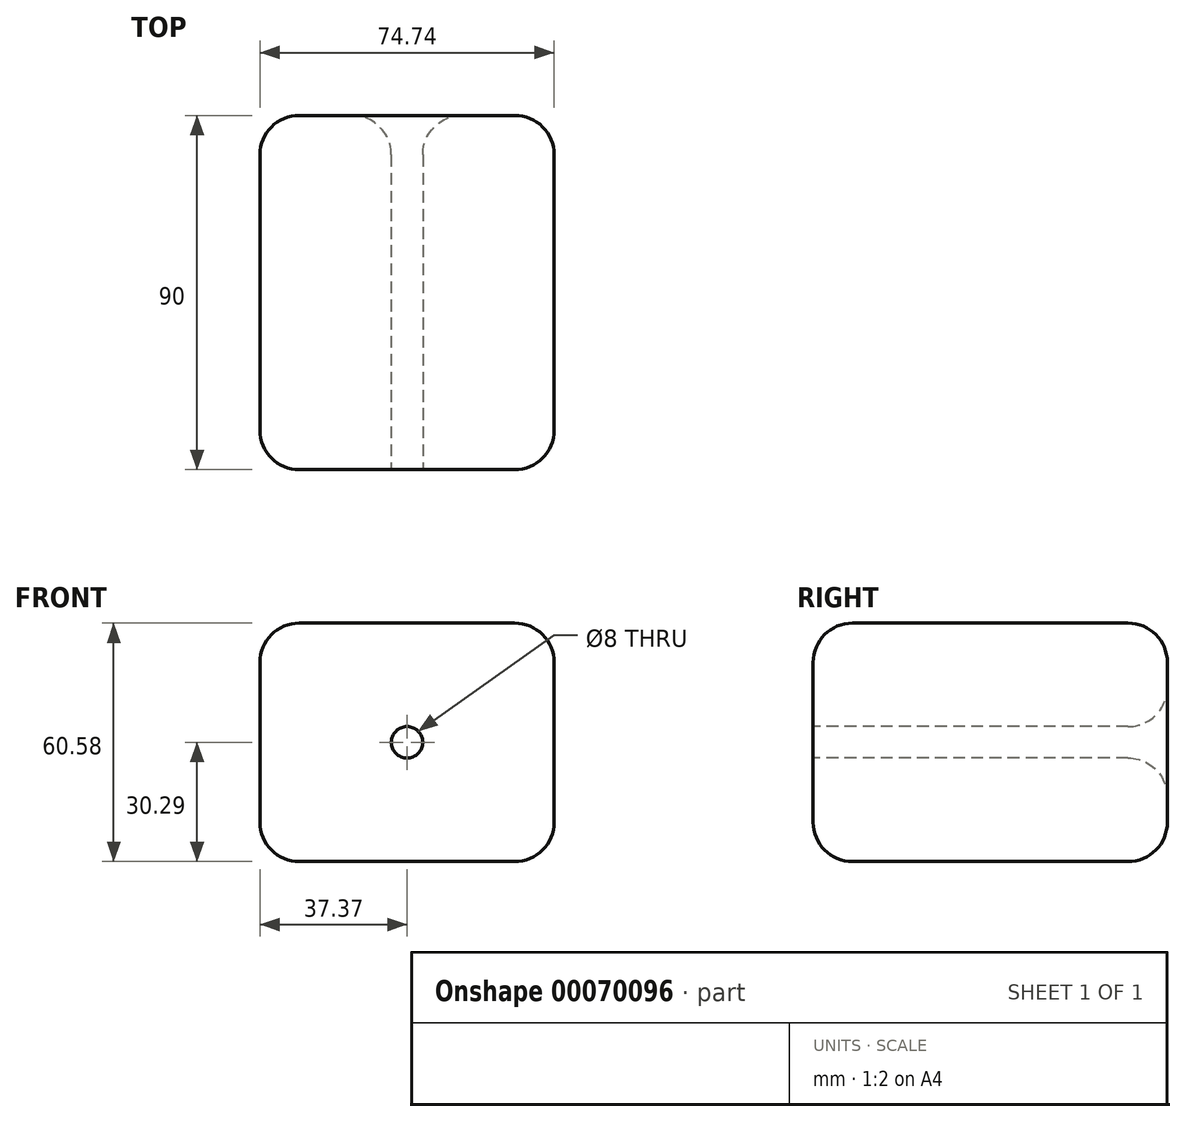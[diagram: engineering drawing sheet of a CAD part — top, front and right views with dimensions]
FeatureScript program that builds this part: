
annotation { "Feature Type Name" : "Feature", "Feature Type Description" : "" }
export const myFeature = defineFeature(function(context is Context, id is Id, definition is map)
    precondition{}
    {
        {
            var Q0;
            Q0=qCreatedBy(makeId("Front.planeOp"),FACE);
            var sketch = newSketch(context, id + "F0", { "sketchPlane" : qUnion([Q0])});
            skLineSegment(sketch, "E0.rect.bottom", {"start": v(-37.37, 30.29) * mm, "end": v(37.37, 30.29) * mm});
            skLineSegment(sketch, "E0.rect.top", {"start": v(-37.37, -30.29) * mm, "end": v(37.37, -30.29) * mm});
            skLineSegment(sketch, "E0.rect.left", {"start": v(-37.37, 30.29) * mm, "end": v(-37.37, -30.29) * mm});
            skLineSegment(sketch, "E0.rect.right", {"start": v(37.37, 30.29) * mm, "end": v(37.37, -30.29) * mm});
            skPoint(sketch, "E0.rect.middle", {"position": v(0, 0) * mm});
            skSolve(sketch);
        }
        {
            var Q0;
            Q0 = qSketchRegion(id + "F0", true);
            extrude(context, id + "F1", {"entities" : qUnion([Q0]), "depth" : 90 * mm});
        }
        {
            var Q0;
            Q0=makeQuery(id+"F1.opExtrude","CAP_FACE",FACE,{"disambiguationData":[OSD([sQuery(id+"F0.wireOp",EDGE,"E0.rect.bottom"),sQuery(id+"F0.wireOp",EDGE,"E0.rect.top"),sQuery(id+"F0.wireOp",EDGE,"E0.rect.left"),sQuery(id+"F0.wireOp",EDGE,"E0.rect.right")])],"isStart":false});
            var sketch = newSketch(context, id + "F2", { "sketchPlane" : qUnion([Q0])});
            skCircle(sketch, "E1", {"center": v(0, 0) * mm, "radius": 4 * mm});
            skSolve(sketch);
        }
        {
            var Q0;
            Q0 = qSketchRegion(id + "F2", true);
            extrude(context, id + "F3", {"entities" : qUnion([Q0]), "operationType" : NewBodyOperationType.REMOVE, "endBound" : BoundingType.THROUGH_ALL, "oppositeDirection" : true, "depth" : 40 * mm});
        }
        {
            var Q0;
            Q0=makeQuery(id+"F1.opExtrude","CAP_EDGE",EDGE,{"disambiguationData":[OSD([sQuery(id+"F0.wireOp",EDGE,"E0.rect.left")])],"isStart":false});
            var Q1;
            Q1=makeQuery(id+"F1.opExtrude","CAP_EDGE",EDGE,{"disambiguationData":[OSD([sQuery(id+"F0.wireOp",EDGE,"E0.rect.right")])],"isStart":false});
            var Q2;
            Q2=makeQuery(id+"F1.opExtrude","CAP_EDGE",EDGE,{"disambiguationData":[OSD([sQuery(id+"F0.wireOp",EDGE,"E0.rect.bottom")])],"isStart":false});
            var Q3;
            Q3=makeQuery(id+"F1.opExtrude","SWEPT_EDGE",EDGE,{"disambiguationData":[OSD([sQuery(id+"F0.wireOp",EDGE,"E0.rect.top"),sQuery(id+"F0.wireOp",EDGE,"E0.rect.left")])]});
            var Q4;
            Q4=makeQuery(id+"F1.opExtrude","SWEPT_EDGE",EDGE,{"disambiguationData":[OSD([sQuery(id+"F0.wireOp",EDGE,"E0.rect.top"),sQuery(id+"F0.wireOp",EDGE,"E0.rect.right")])]});
            var Q5;
            Q5=makeQuery(id+"F1.opExtrude","CAP_EDGE",EDGE,{"disambiguationData":[OSD([sQuery(id+"F0.wireOp",EDGE,"E0.rect.top")])],"isStart":true});
            var Q6;
            Q6=makeQuery(id+"F1.opExtrude","SWEPT_EDGE",EDGE,{"disambiguationData":[OSD([sQuery(id+"F0.wireOp",EDGE,"E0.rect.bottom"),sQuery(id+"F0.wireOp",EDGE,"E0.rect.right")])]});
            var Q7;
            Q7=makeQuery(id+"F1.opExtrude","CAP_EDGE",EDGE,{"disambiguationData":[OSD([sQuery(id+"F0.wireOp",EDGE,"E0.rect.right")])],"isStart":true});
            var Q8;
            Q8=makeQuery(id+"F1.opExtrude","SWEPT_EDGE",EDGE,{"disambiguationData":[OSD([sQuery(id+"F0.wireOp",EDGE,"E0.rect.bottom"),sQuery(id+"F0.wireOp",EDGE,"E0.rect.left")])]});
            var Q9;
            Q9=makeQuery(id+"F1.opExtrude","CAP_EDGE",EDGE,{"disambiguationData":[OSD([sQuery(id+"F0.wireOp",EDGE,"E0.rect.left")])],"isStart":true});
            var Q10;
            Q10=makeQuery(id+"F1.opExtrude","CAP_EDGE",EDGE,{"disambiguationData":[OSD([sQuery(id+"F0.wireOp",EDGE,"E0.rect.bottom")])],"isStart":true});
            var Q11;
            Q11=makeQuery(id+"F3.boolean.opBoolean","COPY",EDGE,{"derivedFrom":makeQuery(id+"F3.opExtrude","CAP_EDGE",EDGE,{"disambiguationData":[OSD([sQuery(id+"F2.wireOp",EDGE,"E1")])],"isStart":true})});
            var Q12;
            Q12=makeQuery(id+"F3.boolean.opBoolean","INTERSECT",EDGE,{"derivedFrom":[makeQuery(id+"F1.opExtrude","CAP_FACE",FACE,{"disambiguationData":[OSD([sQuery(id+"F0.wireOp",EDGE,"E0.rect.bottom"),sQuery(id+"F0.wireOp",EDGE,"E0.rect.top"),sQuery(id+"F0.wireOp",EDGE,"E0.rect.left"),sQuery(id+"F0.wireOp",EDGE,"E0.rect.right")])],"isStart":true}),makeQuery(id+"F3.opExtrude","SWEPT_FACE",FACE,{"disambiguationData":[OSD([sQuery(id+"F2.wireOp",EDGE,"E1")])]})]});
            var Q13;
            Q13=makeQuery(id+"F1.opExtrude","SWEPT_FACE",FACE,{"disambiguationData":[OSD([sQuery(id+"F0.wireOp",EDGE,"E0.rect.top")])]});
            fillet(context, id + "F4", {"entities" : qUnion([Q0, Q1, Q2, Q3, Q4, Q5, Q6, Q7, Q8, Q9, Q10, Q11, Q12, Q13]), "radius" : 10 * mm, "tangentPropagation" : true, "allowEdgeOverflow" : false});
        }
    });
